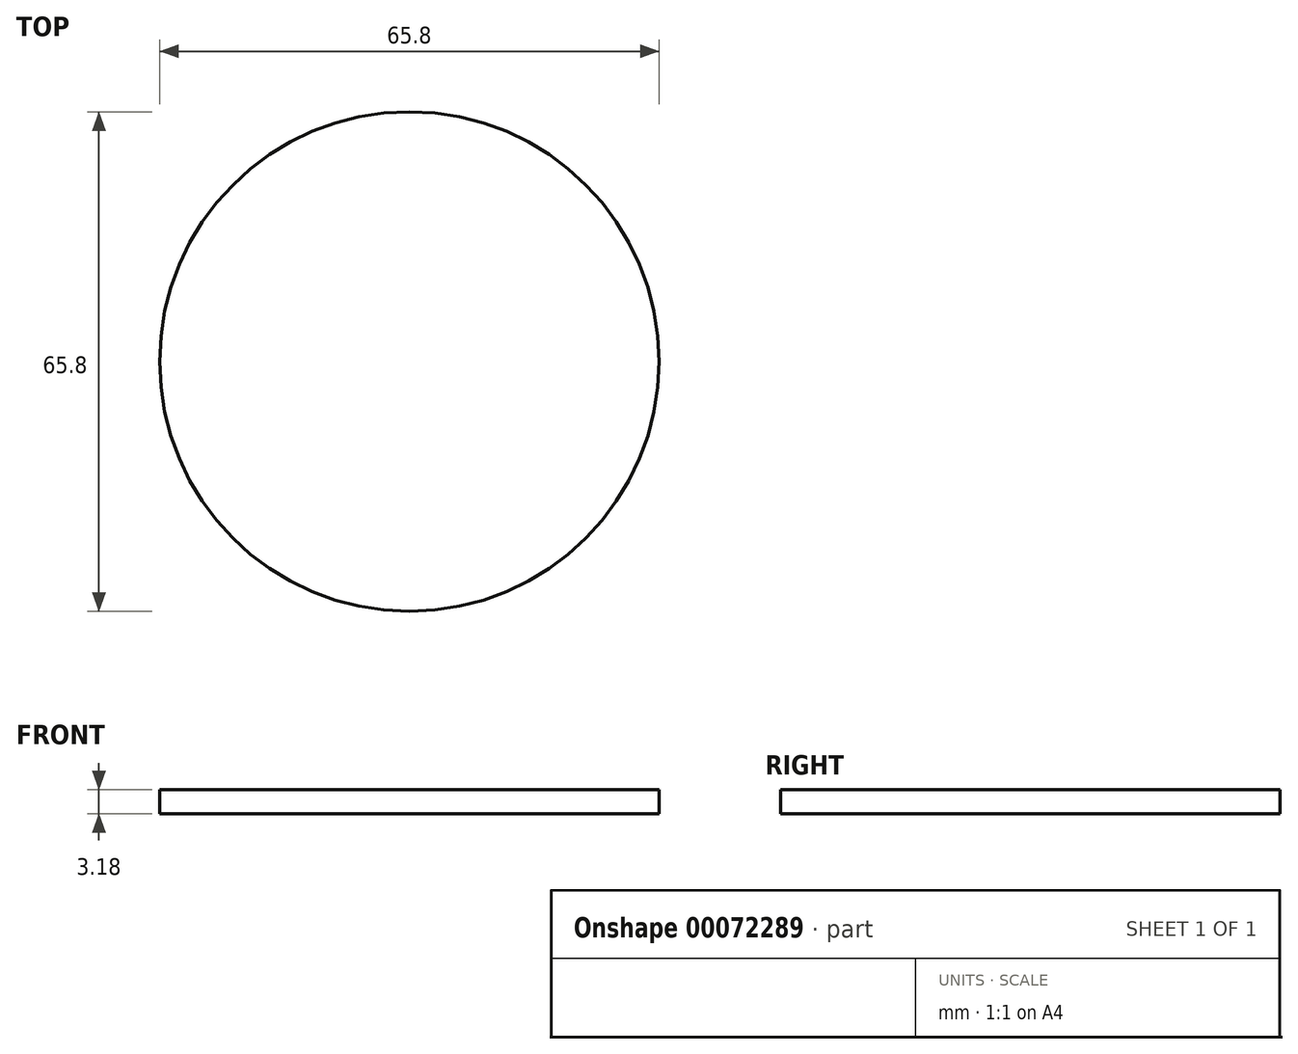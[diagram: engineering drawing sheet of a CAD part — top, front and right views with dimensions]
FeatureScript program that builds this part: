
annotation { "Feature Type Name" : "Feature", "Feature Type Description" : "" }
export const myFeature = defineFeature(function(context is Context, id is Id, definition is map)
    precondition{}
    {
        {
            var Q0;
            Q0=qCreatedBy(makeId("Top.planeOp"),FACE);
            var sketch = newSketch(context, id + "F0", { "sketchPlane" : qUnion([Q0])});
            skCircle(sketch, "E0", {"center": v(0, 0) * mm, "radius": 32.9 * mm});
            skLineSegment(sketch, "E1", {"start": v(0, -32.9) * mm, "end": v(0, -91.23) * mm});
            skSolve(sketch);
        }
        {
            var Q0;
            Q0=makeQuery(id+"F0.imprint","IMPRINT",FACE,{"disambiguationData":[TD([[makeQuery(id+"F0.imprint","IMPRINT",EDGE,{"derivedFrom":sQuery(id+"F0.wireOp",EDGE,"E0")}),1.0]])]});
            extrude(context, id + "F1", {"entities" : qUnion([Q0]), "depth" : 3.17 * mm});
        }
        {
            var Q0;
            Q0=qCreatedBy(makeId("Top.planeOp"),FACE);
            var sketch = newSketch(context, id + "F2", { "sketchPlane" : qUnion([Q0])});
            skLineSegment(sketch, "E2", {"start": v(1.84, -32.93) * mm, "end": v(1.84, -91.24) * mm});
            skSolve(sketch);
        }
        {
            var Q0;
            Q0=sQuery(id+"F2.wireOp",EDGE,"E2");
            extrude(context, id + "F3", {"bodyType" : ToolBodyType.SURFACE, "surfaceEntities" : qUnion([Q0]), "depth" : 0.32 * mm});
        }
        {
            var Q0;
            Q0=sQuery(id+"F0.wireOp",EDGE,"E1");
            extrude(context, id + "F4", {"bodyType" : ToolBodyType.SURFACE, "surfaceEntities" : qUnion([Q0]), "depth" : 0.32 * mm});
        }
    });
